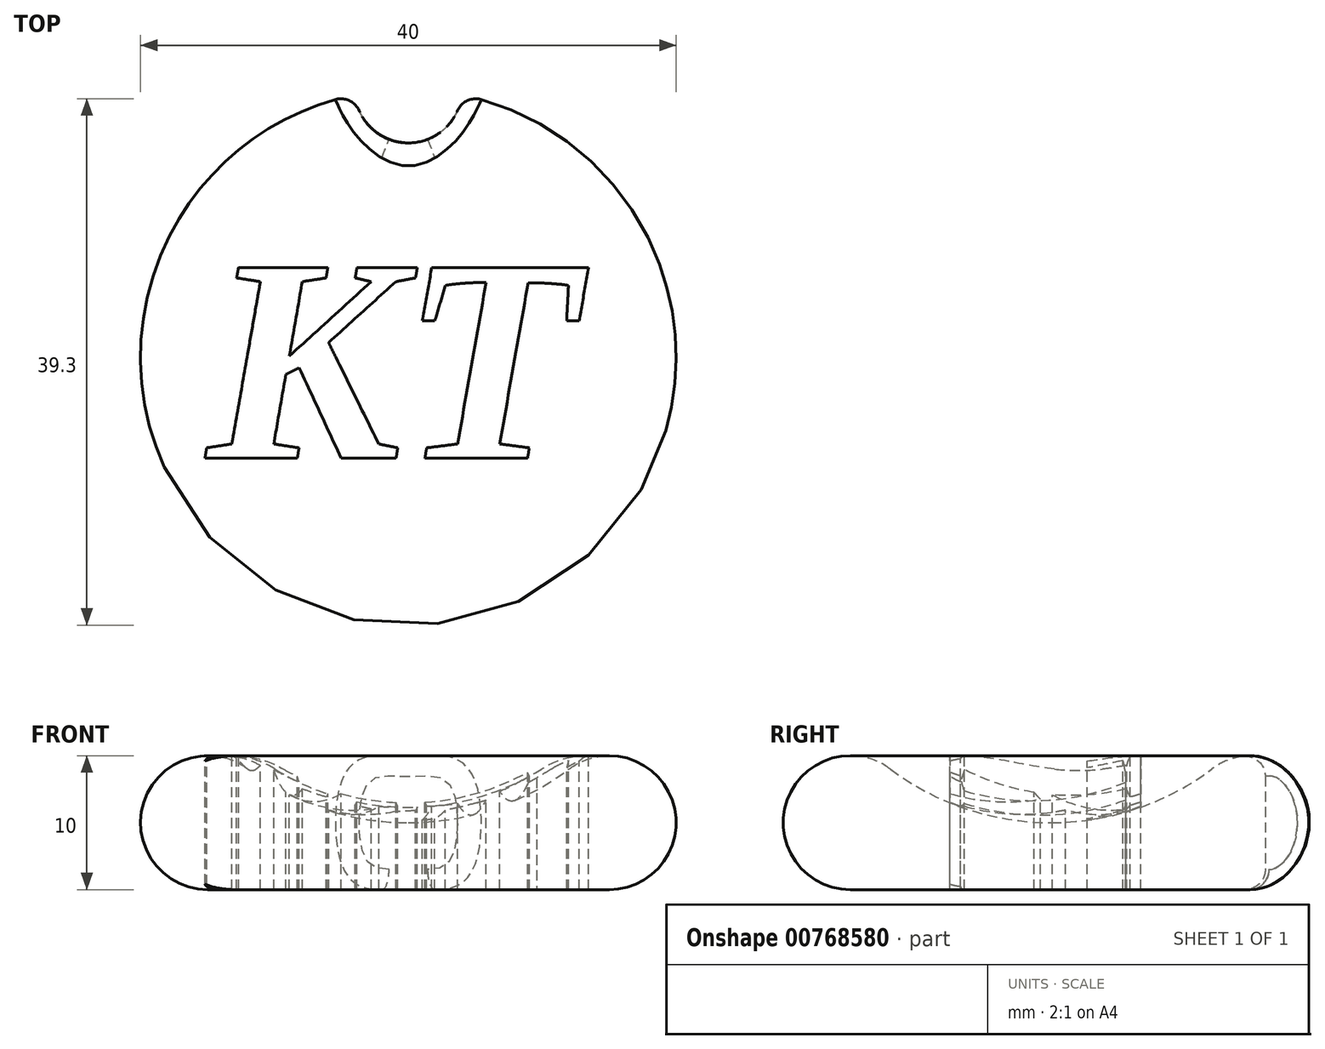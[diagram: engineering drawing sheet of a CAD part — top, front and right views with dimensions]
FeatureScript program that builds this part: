
annotation { "Feature Type Name" : "Feature", "Feature Type Description" : "" }
export const myFeature = defineFeature(function(context is Context, id is Id, definition is map)
    precondition{}
    {
        {
            var Q0;
            Q0=qCreatedBy(makeId("Front.planeOp"),FACE);
            var sketch = newSketch(context, id + "F0", { "sketchPlane" : qUnion([Q0])});
            skArc(sketch, "E0", {"start": v(-12, 9) * mm, "mid": v(-19.74, 6.58) * mm, "end": v(-15, 0) * mm});
            skArc(sketch, "E1", {"start": v(-12, 9) * mm, "mid": v(-6.32, 6.03) * mm, "end": v(0, 5) * mm});
            skLineSegment(sketch, "E2", {"start": v(-15, 0) * mm, "end": v(0, 0) * mm});
            skLineSegment(sketch, "E3", {"start": v(0, 0) * mm, "end": v(0, 5) * mm});
            skSolve(sketch);
        }
        {
            var Q0;
            Q0=makeQuery(id+"F0.imprint","IMPRINT",FACE,{"disambiguationData":[TD([[makeQuery(id+"F0.imprint","IMPRINT",EDGE,{"derivedFrom":sQuery(id+"F0.wireOp",EDGE,"E0")}),1.0]])]});
            var Q1;
            Q1=sQuery(id+"F0.wireOp",EDGE,"E3");
            revolve(context, id + "F1", {"surfaceOperationType" : NewSurfaceOperationType.NEW, "entities" : qUnion([Q0]), "axis" : qUnion([Q1]), "revolveType" : RevolveType.FULL});
        }
        {
            var Q0;
            Q0=qCreatedBy(makeId("Front.planeOp"),FACE);
            var sketch = newSketch(context, id + "F2", { "sketchPlane" : qUnion([Q0])});
            skCircle(sketch, "E4", {"center": v(-15, 5) * mm, "radius": 4 * mm});
            skSolve(sketch);
        }
        {
            var Q0;
            Q0=qSketchRegion(id+"F2",true);
            var Q1;
            Q1=sQuery(id+"F0.wireOp",EDGE,"E3");
            revolve(context, id + "F3", {"operationType" : NewBodyOperationType.ADD, "surfaceOperationType" : NewSurfaceOperationType.NEW, "entities" : qUnion([Q0]), "axis" : qUnion([Q1]), "revolveType" : RevolveType.FULL});
        }
        {
            var Q0;
            Q0=qCreatedBy(makeId("Top.planeOp"),FACE);
            var sketch = newSketch(context, id + "F4", { "sketchPlane" : qUnion([Q0])});
            skCircle(sketch, "E5", {"center": v(0, 20) * mm, "radius": 4 * mm});
            skSolve(sketch);
        }
        {
            var Q0;
            Q0=makeQuery(id+"F4.imprint","IMPRINT",FACE,{"disambiguationData":[TD([[makeQuery(id+"F4.imprint","IMPRINT",EDGE,{"derivedFrom":sQuery(id+"F4.wireOp",EDGE,"E5")}),1.0]])]});
            extrude(context, id + "F5", {"entities" : qUnion([Q0]), "operationType" : NewBodyOperationType.REMOVE, "depth" : 18.8 * mm, "offsetDistance" : 25 * mm});
        }
        {
            var Q0;
            Q0=makeQuery(id+"F5.boolean.opBoolean","INTERSECT",EDGE,{"derivedFrom":[makeQuery(id+"F1.opRevolve","SWEPT_FACE",FACE,{"disambiguationData":[OSD([sQuery(id+"F0.wireOp",EDGE,"E0")])]}),makeQuery(id+"F5.opExtrude","SWEPT_FACE",FACE,{"disambiguationData":[OSD([sQuery(id+"F4.wireOp",EDGE,"E5")])]})]});
            fillet(context, id + "F6", {"entities" : qUnion([Q0]), "radius" : 1.5 * mm, "tangentPropagation" : true, "allowEdgeOverflow" : false});
        }
        {
            var Q0;
            Q0=qCreatedBy(makeId("Top.planeOp"),FACE);
            cPlane(context, id + "F7", {"entities" : qUnion([Q0]), "cplaneType" : CPlaneType.OFFSET, "offset" : 10 * mm, "width" : 150 * mm, "height" : 150 * mm});
        }
        {
            var Q0;
            Q0=qCreatedBy(id+"F7.planeOp",FACE);
            var sketch = newSketch(context, id + "F8", { "sketchPlane" : qUnion([Q0])});
            skText(sketch, "E6", { "text": "KT", "fontName": "Tinos-BoldItalic.ttf"});
            const initialGuessF8  = {"E6": [-0.01503, -0.00754, 1, 0, 0.01565]};
            skSetInitialGuess(sketch, initialGuessF8);
            skSolve(sketch);
        }
        {
            var Q0;
            Q0 = qSketchRegion(id + "F8", true);
            extrude(context, id + "F9", {"entities" : qUnion([Q0]), "operationType" : NewBodyOperationType.REMOVE, "oppositeDirection" : true, "depth" : 25 * mm, "offsetDistance" : 25 * mm});
        }
    });
